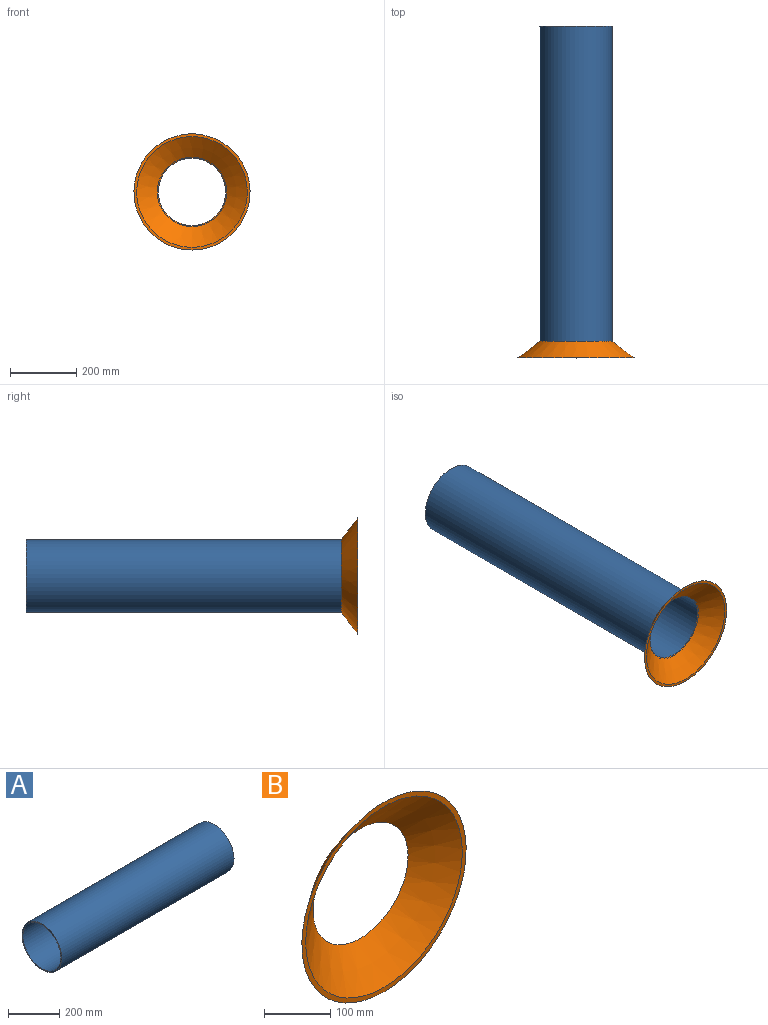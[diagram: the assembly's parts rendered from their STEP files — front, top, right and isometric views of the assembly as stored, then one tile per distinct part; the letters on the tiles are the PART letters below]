
ASSEMBLY  parts=2 mates=1
PART A: 4 faces, bbox 950x219x219 mm
  f0: cylinder r=109.5mm len=950mm, axis (-1,0,0), area 653608.4mm2, adj f1,f2
  f1: plane 219x219mm, normal (1,0,0), area 3361.5mm2, adj f0,f3
  f2: plane 219x219mm, normal (-1,0,0), area 3361.5mm2, adj f0,f3
  f3: cylinder r=104.5mm len=950mm, axis (-1,0,0), area 623763.2mm2, adj f1,f2
PART B: 4 faces, bbox 350x50x350 mm
  f0: plane 219x219mm, normal (0,1,0), area 5456.1mm2, adj f2,f3
  f1: plane 350x350mm, normal (0,-1,0), area 8847.4mm2, adj f2,f3
  f2: cone r=109.5mm half-angle=52.6deg, axis (0,-1,0), area 73650.4mm2, adj f0,f1
  f3: cone r=106.47mm half-angle=52.6deg, axis (0,-1,0), area 69383.9mm2, adj f0,f1
PLACE A rot(axis=(0.58,-0.58,-0.58),120deg) t=(-225,440,0)mm
PLACE B t=(-225,-510,0)mm
MATE fastened A.f0 <-> B.f2  axis (0,-1,0) through (-225,-510,0)mm
